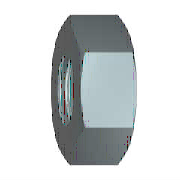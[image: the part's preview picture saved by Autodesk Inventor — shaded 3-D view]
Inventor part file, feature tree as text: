
AUTODESK INVENTOR PART (.ipt)
format: ipt  version: 2022 (Build 260153000, 153)  size: 175,104 bytes
history: native  units: mm (DEFAULTED — no unit token found)
features: sketch x3, other x2, extrude x1, hole x1, plane x1
ambient origin geometry x7: Origin, YZ Plane, XZ Plane, X Axis, Y Axis, Z Axis, Center Point
bodies: Solid1 (feature_tree)
feature tree (8):
  extrude  "Базовый элемент"  Depth=9.237604mm
  other  "Фаска1"
  hole  "Резьба"  [1 undecoded]
  other  "Work Axis1"
  plane  "Work Plane1"
  sketch  "Эскиз1"
  sketch  "Эскиз2"
  sketch  "Эскиз3"
note: 1 required parameter value undecoded (feature->parameter linkage not recoverable at this tier; creation-order binding heuristic only, values carry confidence <= 0.55)
